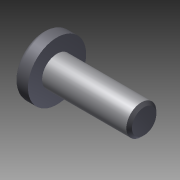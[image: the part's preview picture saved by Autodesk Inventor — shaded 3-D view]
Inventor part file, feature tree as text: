
AUTODESK INVENTOR PART (.ipt)
format: ipt  version: 2015 (Build 190159000, 159)  size: 133,632 bytes
history: native  units: in
note: dims shown in document units (in); Inventor stores cm internally (conversion verified against a paired STEP export)
features: chamfer x1, other x1, imported_body x1
ambient origin geometry x8: Origin, YZ Plane, XZ Plane, XY Plane, X Axis, Y Axis, Z Axis, Center Point
bodies: Body1 (feature_tree)
feature tree (3):
  chamfer  "Chamfer1"  [1 undecoded]
  other  "2-56 X 0.250 PHS (PHS-02)1"
  imported_body  "Base1"
note: 1 required parameter value undecoded (feature->parameter linkage not recoverable at this tier; creation-order binding heuristic only, values carry confidence <= 0.55)
